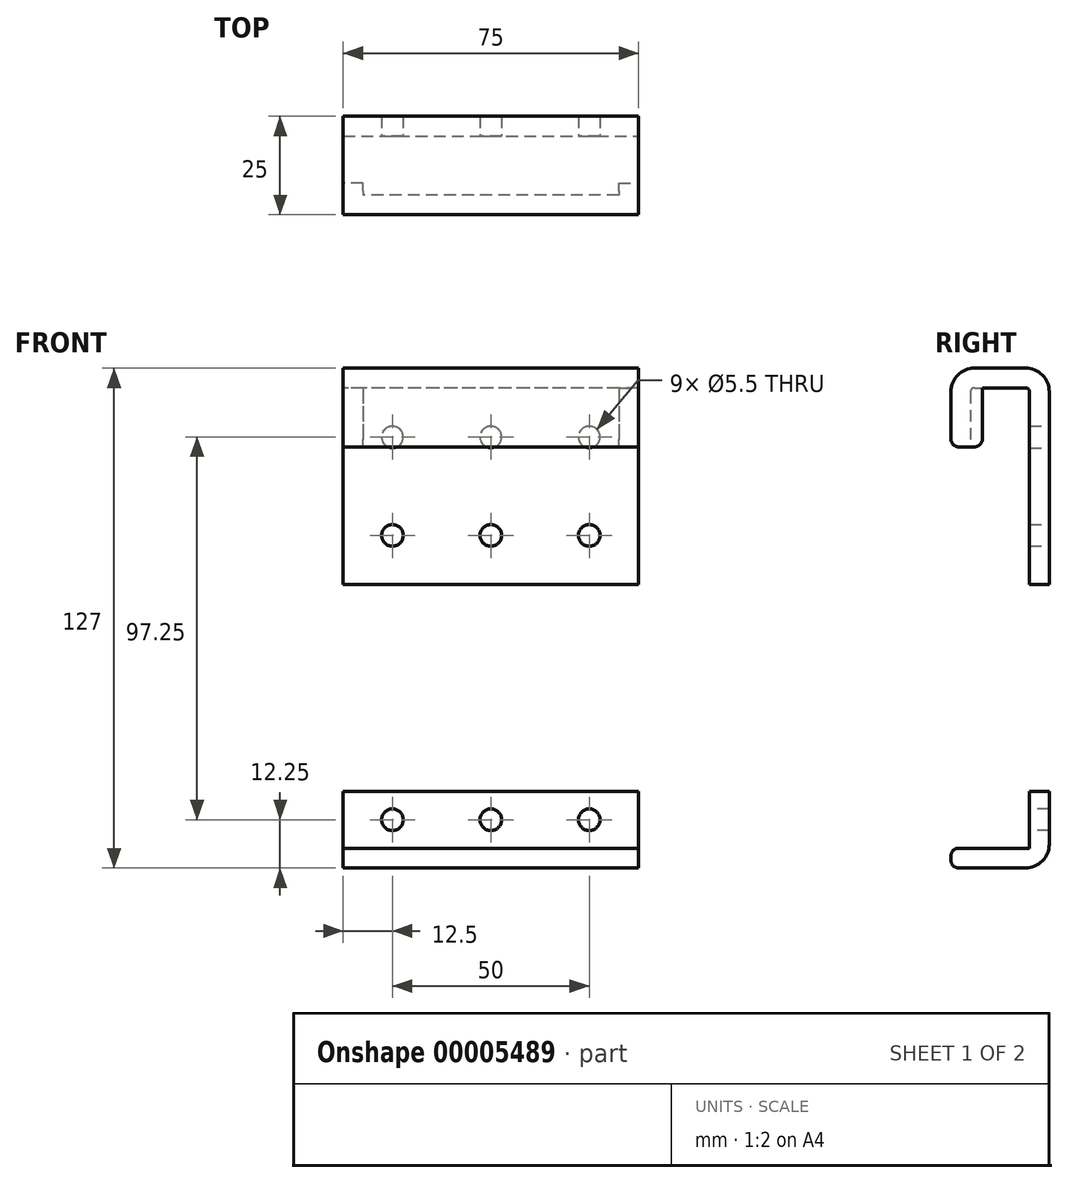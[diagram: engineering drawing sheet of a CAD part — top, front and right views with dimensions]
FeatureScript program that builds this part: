
annotation { "Feature Type Name" : "Feature", "Feature Type Description" : "" }
export const myFeature = defineFeature(function(context is Context, id is Id, definition is map)
    precondition{}
    {
        {
            var Q0;
            Q0=qCreatedBy(makeId("Right.planeOp"),FACE);
            var sketch = newSketch(context, id + "F0", { "sketchPlane" : qUnion([Q0])});
            skLineSegment(sketch, "E0", {"start": v(0, 0) * mm, "end": v(0, 50) * mm});
            skLineSegment(sketch, "E1", {"start": v(0, 50) * mm, "end": v(-15, 50) * mm});
            skLineSegment(sketch, "E2", {"start": v(-15, 50) * mm, "end": v(-15, 35) * mm});
            skLineSegment(sketch, "E3.0", {"start": v(-20, 55) * mm, "end": v(-20, 35) * mm});
            skLineSegment(sketch, "E3.1", {"start": v(5, 55) * mm, "end": v(-20, 55) * mm});
            skLineSegment(sketch, "E3.2", {"start": v(5, 0) * mm, "end": v(5, 55) * mm});
            skLineSegment(sketch, "E4", {"start": v(0, 0) * mm, "end": v(5, 0) * mm});
            skLineSegment(sketch, "E5", {"start": v(-20, 35) * mm, "end": v(-15, 35) * mm});
            skSolve(sketch);
        }
        {
            var Q0;
            Q0=makeQuery(id+"F0.imprint","IMPRINT",FACE,{"disambiguationData":[TD([[makeQuery(id+"F0.imprint","IMPRINT",EDGE,{"derivedFrom":sQuery(id+"F0.wireOp",EDGE,"E0")}),-1.0]])]});
            extrude(context, id + "F1", {"entities" : qUnion([Q0]), "endBound" : BoundingType.SYMMETRIC, "depth" : 75 * mm});
        }
        {
            var Q0;
            Q0=makeQuery(id+"F1.opExtrude","SWEPT_FACE",FACE,{"disambiguationData":[OSD([sQuery(id+"F0.wireOp",EDGE,"E5")])]});
            var sketch = newSketch(context, id + "F2", { "sketchPlane" : qUnion([Q0])});
            skLineSegment(sketch, "E6", {"start": v(0, 0) * mm, "end": v(0, 20) * mm, "construction": true});
            skLineSegment(sketch, "E7", {"start": v(37.5, 15) * mm, "end": v(37.5, 12) * mm});
            skLineSegment(sketch, "E8", {"start": v(37.5, 12) * mm, "end": v(32.5, 12) * mm});
            skLineSegment(sketch, "E9", {"start": v(32.5, 12) * mm, "end": v(32.5, 15) * mm});
            skLineSegment(sketch, "E10.0.MirrorCS", {"start": v(-32.5, 12) * mm, "end": v(-32.5, 15) * mm});
            skLineSegment(sketch, "E11.0.MirrorCS", {"start": v(-37.5, 12) * mm, "end": v(-32.5, 12) * mm});
            skLineSegment(sketch, "E12.0.MirrorCS", {"start": v(-37.5, 15) * mm, "end": v(-37.5, 12) * mm});
            skSolve(sketch);
        }
        {
            var Q0;
            {var subQ2=sQuery(id+"F2.wireOp",EDGE,"E10.0.MirrorCS");Q0=makeQuery(id+"F2.imprint","IMPRINT",FACE,{"disambiguationData":[TD([[makeQuery(id+"F2.imprint","IMPRINT",EDGE,{"derivedFrom":subQ2}),1.0]])]});}
            var Q1;
            {var subQ3=sQuery(id+"F2.wireOp",EDGE,"E7");Q1=makeQuery(id+"F2.imprint","IMPRINT",FACE,{"disambiguationData":[TD([[makeQuery(id+"F2.imprint","IMPRINT",EDGE,{"derivedFrom":subQ3}),-1.0]])]});}
            var Q2;
            Q2=makeQuery(id+"F1.opExtrude","SWEPT_FACE",FACE,{"disambiguationData":[OSD([sQuery(id+"F0.wireOp",EDGE,"E1")])]});
            extrude(context, id + "F3", {"entities" : qUnion([Q0, Q1]), "operationType" : NewBodyOperationType.ADD, "endBound" : BoundingType.UP_TO_SURFACE, "oppositeDirection" : true, "endBoundEntityFace" : qUnion([Q2]), "depth" : 25 * mm});
        }
        {
            var Q0;
            Q0=makeQuery(id+"F1.opExtrude","SWEPT_FACE",FACE,{"disambiguationData":[OSD([sQuery(id+"F0.wireOp",EDGE,"E3.2")])]});
            var sketch = newSketch(context, id + "F4", { "sketchPlane" : qUnion([Q0])});
            skLineSegment(sketch, "E13.0", {"start": v(-37.5, 50) * mm, "end": v(37.5, 50) * mm});
            skLineSegment(sketch, "E14", {"start": v(0, 0) * mm, "end": v(0, 50) * mm, "construction": true});
            skLineSegment(sketch, "E15", {"start": v(-37.5, 25) * mm, "end": v(37.5, 25) * mm, "construction": true});
            skPoint(sketch, "E16", {"position": v(0, 25) * mm});
            skCircle(sketch, "E17", {"center": v(-25, 37.5) * mm, "radius": 2.75 * mm});
            skCircle(sketch, "E18.0.1.0", {"center": v(-25, 12.5) * mm, "radius": 2.75 * mm});
            skCircle(sketch, "E18.1.0.0", {"center": v(0, 37.5) * mm, "radius": 2.75 * mm});
            skCircle(sketch, "E18.1.1.0", {"center": v(0, 12.5) * mm, "radius": 2.75 * mm});
            skCircle(sketch, "E18.2.0.0", {"center": v(25, 37.5) * mm, "radius": 2.75 * mm});
            skCircle(sketch, "E18.2.1.0", {"center": v(25, 12.5) * mm, "radius": 2.75 * mm});
            skLineSegment(sketch, "E18.direction1", {"start": v(-25, 37.5) * mm, "end": v(0, 37.5) * mm, "construction": true});
            skLineSegment(sketch, "E18.direction2", {"start": v(-25, 37.5) * mm, "end": v(-25, 12.5) * mm, "construction": true});
            skPoint(sketch, "E19", {"position": v(-25, 25) * mm});
            skSolve(sketch);
        }
        {
            var Q0;
            Q0 = qSketchRegion(id + "F4", true);
            extrude(context, id + "F5", {"entities" : qUnion([Q0]), "operationType" : NewBodyOperationType.REMOVE, "oppositeDirection" : true, "depth" : 5 * mm});
        }
        {
            var Q0;
            Q0=qCreatedBy(makeId("Front.planeOp"),FACE);
            var sketch = newSketch(context, id + "F6", { "sketchPlane" : qUnion([Q0])});
            skLineSegment(sketch, "E20", {"start": v(-37.5, -67) * mm, "end": v(37.5, -67) * mm});
            skLineSegment(sketch, "E21", {"start": v(0, 0) * mm, "end": v(0, -67) * mm, "construction": true});
            skLineSegment(sketch, "E22", {"start": v(-37.5, -52.5) * mm, "end": v(37.5, -52.5) * mm});
            skLineSegment(sketch, "E23", {"start": v(-37.5, -52.5) * mm, "end": v(-37.5, -67) * mm});
            skLineSegment(sketch, "E24", {"start": v(-37.5, -72) * mm, "end": v(37.5, -72) * mm});
            skLineSegment(sketch, "E25", {"start": v(37.5, -67) * mm, "end": v(37.5, -52.5) * mm});
            skCircle(sketch, "E26", {"center": v(-25, -59.75) * mm, "radius": 2.75 * mm});
            skCircle(sketch, "E27.1.0.0", {"center": v(0, -59.75) * mm, "radius": 2.75 * mm});
            skCircle(sketch, "E27.2.0.0", {"center": v(25, -59.75) * mm, "radius": 2.75 * mm});
            skLineSegment(sketch, "E27.direction1", {"start": v(-25, -59.75) * mm, "end": v(0, -59.75) * mm, "construction": true});
            skLineSegment(sketch, "E28", {"start": v(37.5, -67) * mm, "end": v(37.5, -72) * mm});
            skLineSegment(sketch, "E29", {"start": v(-37.5, -67) * mm, "end": v(-37.5, -72) * mm});
            skPoint(sketch, "E30", {"position": v(-37.5, -59.75) * mm});
            skLineSegment(sketch, "E31.0", {"start": v(37.5, 50) * mm, "end": v(-37.5, 50) * mm});
            skSolve(sketch);
        }
        {
            var Q0;
            Q0=makeQuery(id+"F6.imprint","IMPRINT",FACE,{"disambiguationData":[TD([[makeQuery(id+"F6.imprint","IMPRINT",EDGE,{"derivedFrom":sQuery(id+"F6.wireOp",EDGE,"E20")}),1.0]])]});
            var Q1;
            Q1=makeQuery(id+"F6.imprint","IMPRINT",FACE,{"disambiguationData":[TD([[makeQuery(id+"F6.imprint","IMPRINT",EDGE,{"derivedFrom":sQuery(id+"F6.wireOp",EDGE,"E20")}),-1.0]])]});
            extrude(context, id + "F7", {"entities" : qUnion([Q0, Q1]), "oppositeDirection" : true, "depth" : 5 * mm});
        }
        {
            var Q0;
            Q0=makeQuery(id+"F6.imprint","IMPRINT",FACE,{"disambiguationData":[TD([[makeQuery(id+"F6.imprint","IMPRINT",EDGE,{"derivedFrom":sQuery(id+"F6.wireOp",EDGE,"E20")}),-1.0]])]});
            extrude(context, id + "F8", {"entities" : qUnion([Q0]), "operationType" : NewBodyOperationType.ADD, "depth" : 20 * mm});
        }
        {
            var Q0;
            Q0=makeQuery(id+"F1.opExtrude","SWEPT_EDGE",EDGE,{"disambiguationData":[OSD([sQuery(id+"F0.wireOp",EDGE,"E1"),sQuery(id+"F0.wireOp",EDGE,"E2")])]});
            var Q1;
            Q1=makeQuery(id+"F1.opExtrude","SWEPT_EDGE",EDGE,{"disambiguationData":[OSD([sQuery(id+"F0.wireOp",EDGE,"E0"),sQuery(id+"F0.wireOp",EDGE,"E1")])]});
            var Q2;
            Q2=makeQuery(id+"F3.opExtrude","SWEPT_EDGE",EDGE,{"disambiguationData":[OSD([sQuery(id+"F0.wireOp",EDGE,"E2"),sQuery(id+"F0.wireOp",EDGE,"E5"),sQuery(id+"F2.wireOp",EDGE,"E9")])]});
            var Q3;
            Q3=makeQuery(id+"F3.opExtrude","CAP_EDGE",EDGE,{"disambiguationData":[OSD([sQuery(id+"F2.wireOp",EDGE,"E9")])],"isStart":false});
            var Q4;
            Q4=makeQuery(id+"F3.opExtrude","SWEPT_EDGE",EDGE,{"disambiguationData":[OSD([sQuery(id+"F0.wireOp",EDGE,"E2"),sQuery(id+"F0.wireOp",EDGE,"E5"),sQuery(id+"F2.wireOp",EDGE,"E10.0.MirrorCS")])]});
            var Q5;
            Q5=makeQuery(id+"F3.opExtrude","CAP_EDGE",EDGE,{"disambiguationData":[OSD([sQuery(id+"F2.wireOp",EDGE,"E10.0.MirrorCS")])],"isStart":false});
            var Q6;
            Q6=makeQuery(id+"F3.opExtrude","CAP_EDGE",EDGE,{"disambiguationData":[OSD([sQuery(id+"F2.wireOp",EDGE,"E8")])],"isStart":false});
            var Q7;
            Q7=makeQuery(id+"F3.opExtrude","CAP_EDGE",EDGE,{"disambiguationData":[OSD([sQuery(id+"F2.wireOp",EDGE,"E11.0.MirrorCS")])],"isStart":false});
            var Q8;
            Q8=makeQuery(id+"F8.opExtrude","CAP_EDGE",EDGE,{"disambiguationData":[OSD([sQuery(id+"F6.wireOp",EDGE,"E20")])],"isStart":true});
            fillet(context, id + "F9", {"entities" : qUnion([Q0, Q1, Q2, Q3, Q4, Q5, Q6, Q7, Q8]), "radius" : 1 * mm, "tangentPropagation" : true, "allowEdgeOverflow" : false});
        }
        {
            var Q0;
            Q0=makeQuery(id+"F1.opExtrude","SWEPT_EDGE",EDGE,{"disambiguationData":[OSD([sQuery(id+"F0.wireOp",EDGE,"E3.0"),sQuery(id+"F0.wireOp",EDGE,"E3.1")])]});
            var Q1;
            Q1=makeQuery(id+"F1.opExtrude","SWEPT_EDGE",EDGE,{"disambiguationData":[OSD([sQuery(id+"F0.wireOp",EDGE,"E3.1"),sQuery(id+"F0.wireOp",EDGE,"E3.2")])]});
            var Q2;
            Q2=makeQuery(id+"F7.opExtrude","CAP_EDGE",EDGE,{"disambiguationData":[OSD([sQuery(id+"F6.wireOp",EDGE,"E24")])],"isStart":false});
            fillet(context, id + "F10", {"entities" : qUnion([Q0, Q1, Q2]), "radius" : 6 * mm, "tangentPropagation" : true, "allowEdgeOverflow" : false});
        }
        {
            var Q0;
            Q0=makeQuery(id+"F1.opExtrude","SWEPT_EDGE",EDGE,{"disambiguationData":[OSD([sQuery(id+"F0.wireOp",EDGE,"E3.0"),sQuery(id+"F0.wireOp",EDGE,"E5")])]});
            var Q1;
            Q1=makeQuery(id+"F3.opExtrude","CAP_EDGE",EDGE,{"disambiguationData":[OSD([sQuery(id+"F2.wireOp",EDGE,"E8")])],"isStart":true});
            var Q2;
            Q2=makeQuery(id+"F3.opExtrude","CAP_EDGE",EDGE,{"disambiguationData":[OSD([sQuery(id+"F2.wireOp",EDGE,"E11.0.MirrorCS")])],"isStart":true});
            var Q3;
            Q3=makeQuery(id+"F8.opExtrude","CAP_EDGE",EDGE,{"disambiguationData":[OSD([sQuery(id+"F6.wireOp",EDGE,"E20")])],"isStart":false});
            var Q4;
            Q4=makeQuery(id+"F8.opExtrude","CAP_EDGE",EDGE,{"disambiguationData":[OSD([sQuery(id+"F6.wireOp",EDGE,"E24")])],"isStart":false});
            fillet(context, id + "F11", {"entities" : qUnion([Q0, Q1, Q2, Q3, Q4]), "radius" : 2 * mm, "tangentPropagation" : true, "allowEdgeOverflow" : false});
        }
    });
